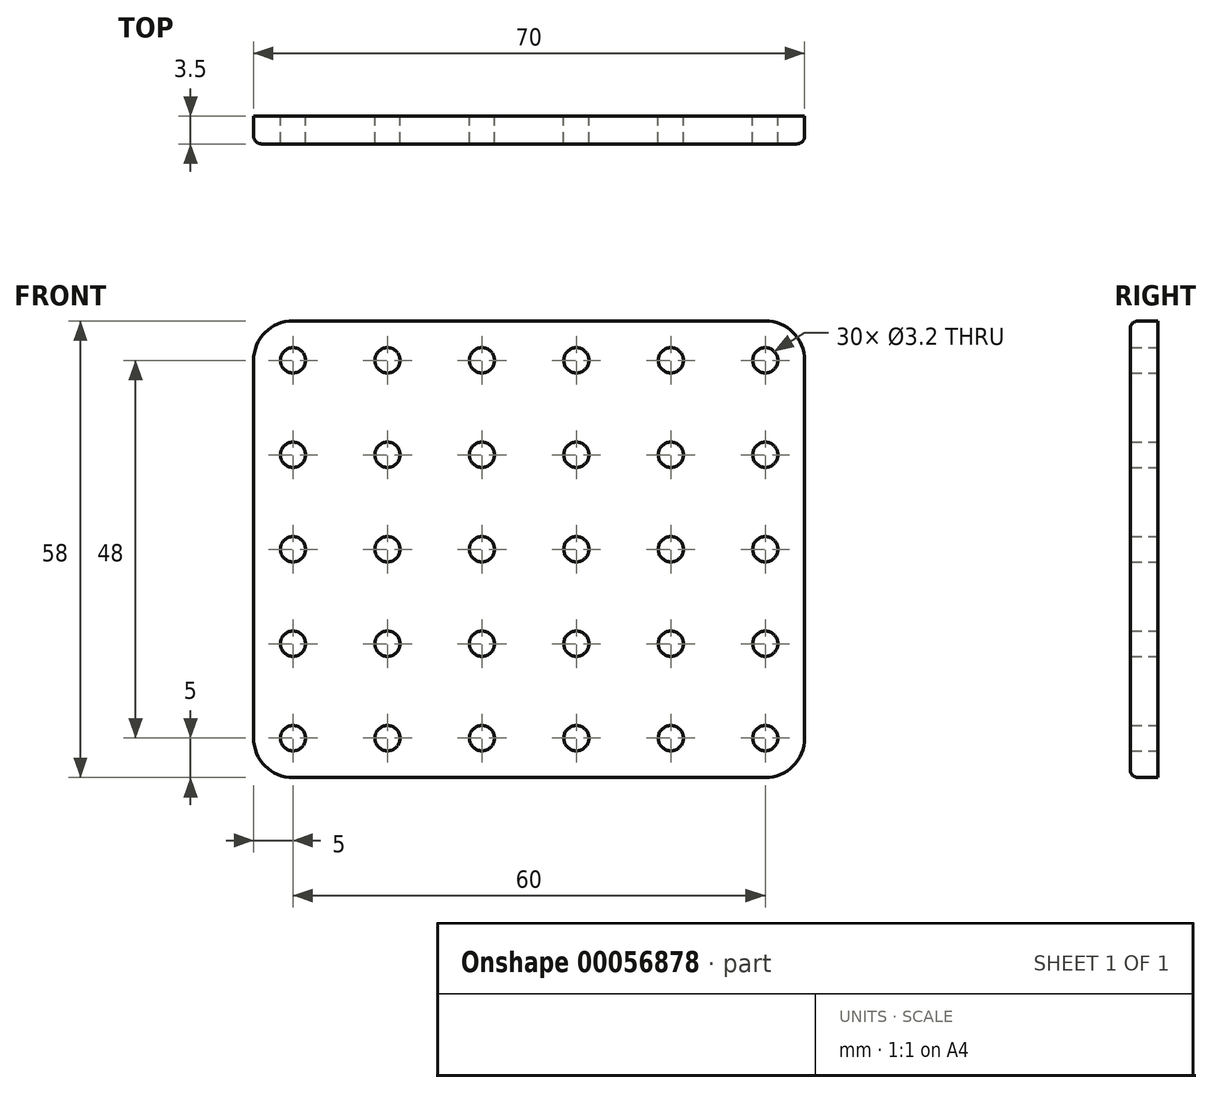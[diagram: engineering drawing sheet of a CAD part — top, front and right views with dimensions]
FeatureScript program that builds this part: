
annotation { "Feature Type Name" : "Feature", "Feature Type Description" : "" }
export const myFeature = defineFeature(function(context is Context, id is Id, definition is map)
    precondition{}
    {
        {
            var Q0;
            Q0=qCreatedBy(makeId("Front.planeOp"),FACE);
            var sketch = newSketch(context, id + "F0", { "sketchPlane" : qUnion([Q0])});
            skLineSegment(sketch, "E0.bottom", {"start": v(-17, 5) * mm, "end": v(53, 5) * mm});
            skLineSegment(sketch, "E0.top", {"start": v(-17, -5) * mm, "end": v(53, -5) * mm});
            skLineSegment(sketch, "E0.left", {"start": v(-17, 5) * mm, "end": v(-17, -5) * mm});
            skLineSegment(sketch, "E0.right", {"start": v(53, 5) * mm, "end": v(53, -5) * mm});
            skLineSegment(sketch, "E1.0", {"start": v(-17, 0) * mm, "end": v(17, 0) * mm, "construction": true});
            skLineSegment(sketch, "E2.0", {"start": v(-12, 5) * mm, "end": v(-12, -5) * mm, "construction": true});
            skLineSegment(sketch, "E3.0", {"start": v(0, 5) * mm, "end": v(0, -5) * mm, "construction": true});
            skLineSegment(sketch, "E4.0", {"start": v(12, 5) * mm, "end": v(12, -5) * mm, "construction": true});
            skCircle(sketch, "E5", {"center": v(-12, 0) * mm, "radius": 1.6 * mm});
            skCircle(sketch, "E6", {"center": v(0, 0) * mm, "radius": 1.6 * mm});
            skCircle(sketch, "E7", {"center": v(12, 0) * mm, "radius": 1.6 * mm});
            skLineSegment(sketch, "E8.0", {"start": v(-17, 53) * mm, "end": v(53, 53) * mm});
            skCircle(sketch, "E9.0.1.0", {"center": v(12, 12) * mm, "radius": 1.6 * mm});
            skCircle(sketch, "E9.0.1.1", {"center": v(0, 12) * mm, "radius": 1.6 * mm});
            skCircle(sketch, "E9.0.1.2", {"center": v(-12, 12) * mm, "radius": 1.6 * mm});
            skCircle(sketch, "E9.0.2.0", {"center": v(12, 24) * mm, "radius": 1.6 * mm});
            skCircle(sketch, "E9.0.2.1", {"center": v(0, 24) * mm, "radius": 1.6 * mm});
            skCircle(sketch, "E9.0.2.2", {"center": v(-12, 24) * mm, "radius": 1.6 * mm});
            skCircle(sketch, "E9.0.3.0", {"center": v(12, 36) * mm, "radius": 1.6 * mm});
            skCircle(sketch, "E9.0.3.1", {"center": v(0, 36) * mm, "radius": 1.6 * mm});
            skCircle(sketch, "E9.0.3.2", {"center": v(-12, 36) * mm, "radius": 1.6 * mm});
            skCircle(sketch, "E9.1.0.0", {"center": v(48, 0) * mm, "radius": 1.6 * mm});
            skCircle(sketch, "E9.1.0.1", {"center": v(36, 0) * mm, "radius": 1.6 * mm});
            skCircle(sketch, "E9.1.0.2", {"center": v(24, 0) * mm, "radius": 1.6 * mm});
            skCircle(sketch, "E9.1.1.0", {"center": v(48, 12) * mm, "radius": 1.6 * mm});
            skCircle(sketch, "E9.1.1.1", {"center": v(36, 12) * mm, "radius": 1.6 * mm});
            skCircle(sketch, "E9.1.1.2", {"center": v(24, 12) * mm, "radius": 1.6 * mm});
            skCircle(sketch, "E9.1.2.0", {"center": v(48, 24) * mm, "radius": 1.6 * mm});
            skCircle(sketch, "E9.1.2.1", {"center": v(36, 24) * mm, "radius": 1.6 * mm});
            skCircle(sketch, "E9.1.2.2", {"center": v(24, 24) * mm, "radius": 1.6 * mm});
            skCircle(sketch, "E9.1.3.0", {"center": v(48, 36) * mm, "radius": 1.6 * mm});
            skCircle(sketch, "E9.1.3.1", {"center": v(36, 36) * mm, "radius": 1.6 * mm});
            skCircle(sketch, "E9.1.3.2", {"center": v(24, 36) * mm, "radius": 1.6 * mm});
            skLineSegment(sketch, "E9.direction1", {"start": v(12, 0) * mm, "end": v(48, 0) * mm, "construction": true});
            skLineSegment(sketch, "E9.direction2", {"start": v(12, 0) * mm, "end": v(12, 12) * mm, "construction": true});
            skCircle(sketch, "E10.0.0.4", {"center": v(12, 48) * mm, "radius": 1.6 * mm});
            skCircle(sketch, "E10.2.0.4", {"center": v(0, 48) * mm, "radius": 1.6 * mm});
            skCircle(sketch, "E10.4.0.4", {"center": v(-12, 48) * mm, "radius": 1.6 * mm});
            skCircle(sketch, "E10.0.1.4", {"center": v(48, 48) * mm, "radius": 1.6 * mm});
            skCircle(sketch, "E10.2.1.4", {"center": v(36, 48) * mm, "radius": 1.6 * mm});
            skCircle(sketch, "E10.4.1.4", {"center": v(24, 48) * mm, "radius": 1.6 * mm});
            skLineSegment(sketch, "E11", {"start": v(-17, 53) * mm, "end": v(-17, 5) * mm});
            skLineSegment(sketch, "E12", {"start": v(53, 53) * mm, "end": v(53, 5) * mm});
            skSolve(sketch);
        }
        {
            var Q0;
            Q0=makeQuery(id+"F0.imprint","IMPRINT",FACE,{"disambiguationData":[TD([[makeQuery(id+"F0.imprint","IMPRINT",EDGE,{"derivedFrom":sQuery(id+"F0.wireOp",EDGE,"E0.bottom")}),1.0]])]});
            var Q1;
            Q1=makeQuery(id+"F0.imprint","IMPRINT",FACE,{"disambiguationData":[TD([[makeQuery(id+"F0.imprint","IMPRINT",EDGE,{"derivedFrom":sQuery(id+"F0.wireOp",EDGE,"E0.bottom")}),-1.0]])]});
            extrude(context, id + "F1", {"entities" : qUnion([Q0, Q1]), "depth" : 3.5 * mm});
        }
        {
            var Q0;
            Q0=makeQuery(id+"F1.opExtrude","SWEPT_EDGE",EDGE,{"disambiguationData":[OSD([sQuery(id+"F0.wireOp",EDGE,"E0.top"),sQuery(id+"F0.wireOp",EDGE,"E0.left")])]});
            var Q1;
            Q1=makeQuery(id+"F1.opExtrude","SWEPT_EDGE",EDGE,{"disambiguationData":[OSD([sQuery(id+"F0.wireOp",EDGE,"E0.top"),sQuery(id+"F0.wireOp",EDGE,"E0.right")])]});
            var Q2;
            Q2=makeQuery(id+"F1.opExtrude","SWEPT_EDGE",EDGE,{"disambiguationData":[OSD([sQuery(id+"F0.wireOp",EDGE,"E8.0"),sQuery(id+"F0.wireOp",EDGE,"E11")])]});
            var Q3;
            Q3=makeQuery(id+"F1.opExtrude","SWEPT_EDGE",EDGE,{"disambiguationData":[OSD([sQuery(id+"F0.wireOp",EDGE,"E8.0"),sQuery(id+"F0.wireOp",EDGE,"E12")])]});
            fillet(context, id + "F2", {"entities" : qUnion([Q0, Q1, Q2, Q3]), "radius" : 5 * mm, "tangentPropagation" : true, "allowEdgeOverflow" : false});
        }
        {
            var Q0;
            Q0=makeQuery(id+"F1.opExtrude","CAP_EDGE",EDGE,{"disambiguationData":[OSD([sQuery(id+"F0.wireOp",EDGE,"E8.0")])],"isStart":false});
            fillet(context, id + "F3", {"entities" : qUnion([Q0]), "radius" : 1 * mm, "tangentPropagation" : true, "allowEdgeOverflow" : false});
        }
    });
